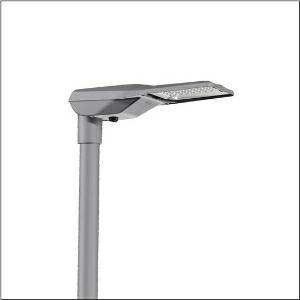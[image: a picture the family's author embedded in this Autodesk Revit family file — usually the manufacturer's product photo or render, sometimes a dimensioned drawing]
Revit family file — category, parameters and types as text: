
# Revit family: streetlight_sl_21_iq_mini___st1_0ab_5xe2m31u08jb_1fa0
name_source: partatom
category: Lighting Fixtures
units: mm (PartAtom-declared; Revit-internal decimal feet)

## family parameters
Cut with Voids When Loaded = No
Host = Face
Light Source = No
Part Type = Normal
Room Calculation Point = No
Round Connector Dimension = Use Diameter
Shared = No

## types (1)
- --- (1 x LED, 9870 lm, 72.5 W, 3000K)
    Apparent Load = 73 VA
    CIE Flux Codes = 40 74 97 100 100
    Color Rendering = 70
    Color Temperature = 3000K
    Default Elevation = 1800 mm
    Description = Streetlight SL 21 iQ mini, mast luminaire, primary light control with lens, of PMMA, primary optical cover: cover, of toughened safety glass, transparent, light distribution: ST1.0aB, light emission: direct distribution, primary light characteristic: asymmetric, installation type: post-top, side-entry, LED, High Power LED, rated luminous flux: 9.870lm, luminous efficacy: 136lm/W, light colour: 730, colour temperature: 3000K, control gear: iQ-Street Remote, D4i with power reduction, control: pre-setting: logarithmic dimming characteristic, Street-Remote, Auto-Match, Temp-Guard, Lumen-Switch, Night-Set, Smart-Wire, Light-Fading, Desk-Remote (wireless, voltage-free reading and setting of iQ features in the workshop via application-optimized NFC function/RFID function), optimised constant luminous flux control (CLO 2.0), mains connection: 220..240V, AC, 50/60Hz, start of lifetime: 73W, end of service life: 76W, reduction: 33W, luminaire housing, of diecast aluminium, powder-coated, SITECO metallic grey (DB 702S), corrosivity category C5 high according to DIN EN ISO 12944, please order mast flange separately, inclination adjustable: 0°, 5°, 10°, 15°, sealing non-destructively replaceable, multi-level sealing system, length: 628mm, width: 235mm, height: 110mm, mast flange for spigot size: 42mm (side-entry): 5XC10008XM4, 60/48mm (side-entry/post-top): 5XC10108XM2, 76/60mm (side-entry/post-top): 5XC10108XM1, mounting height: 4..8m, Smart Interface below, protection rating (complete): IP66, insulation class (complete): insulation class II (safety insulation), certification: CE, ENEC, ENEC+, VDE, impact resistance: IK10, permissible operating ambient temperature for outdoor applications: -40..+50°C, standard-compliant lighting for roads and squares, packaging unit: 1 piece

Light Distribution: ST1.0aB
    Height = 110 mm
    Lamp = 1 x LED
    Lamp Light Flux = 9870 lm
    Lamp Power = 72.5 W
    Lamp count = 1
    Length = 625 mm
    Luminous efficacy = 136 lm/W
    Manufacturer = Siteco
    ModVariant = No
    Model = 5XE2M31U08JB
    Number of Poles = 1
    OnlyDefault = Yes
    Power Factor = 1
    Product Name = Streetlight SL 21 iQ mini | ST1.0aB
    Product group = mast luminaire | pylon top
    ProductGroupID = 6100
    Protection Class = Protection class II
    Protection Degree = IP 66
    RLX_Detail_Level = 1
    RLX_Emergency_Light_Flux = 0 lm
    RLX_Emergency_Type = 0
    RLX_Emergency_Type_DB = No
    RlxData = <blob elided: 92457 chars, md5=ef723d3c>
    Socket = socket
    Standby Power = 0 W
    System Light Flux = 9870 lm
    System Power = 73 W
    Type Comments = factory setting: luminous flux: 100 % | dim-lin: 254 | 755 mA
    Type Image = l_1003516.jpg
    URL = http://relux.com
    VarID = @adj_112239
    Voltage = 0 V
    Weight = 0.00 kg
    Width = 234 mm

## geometry (parser evidence)
native form markers: Blend x4, Sweep x11
no freeform markers — native parametric forms only
